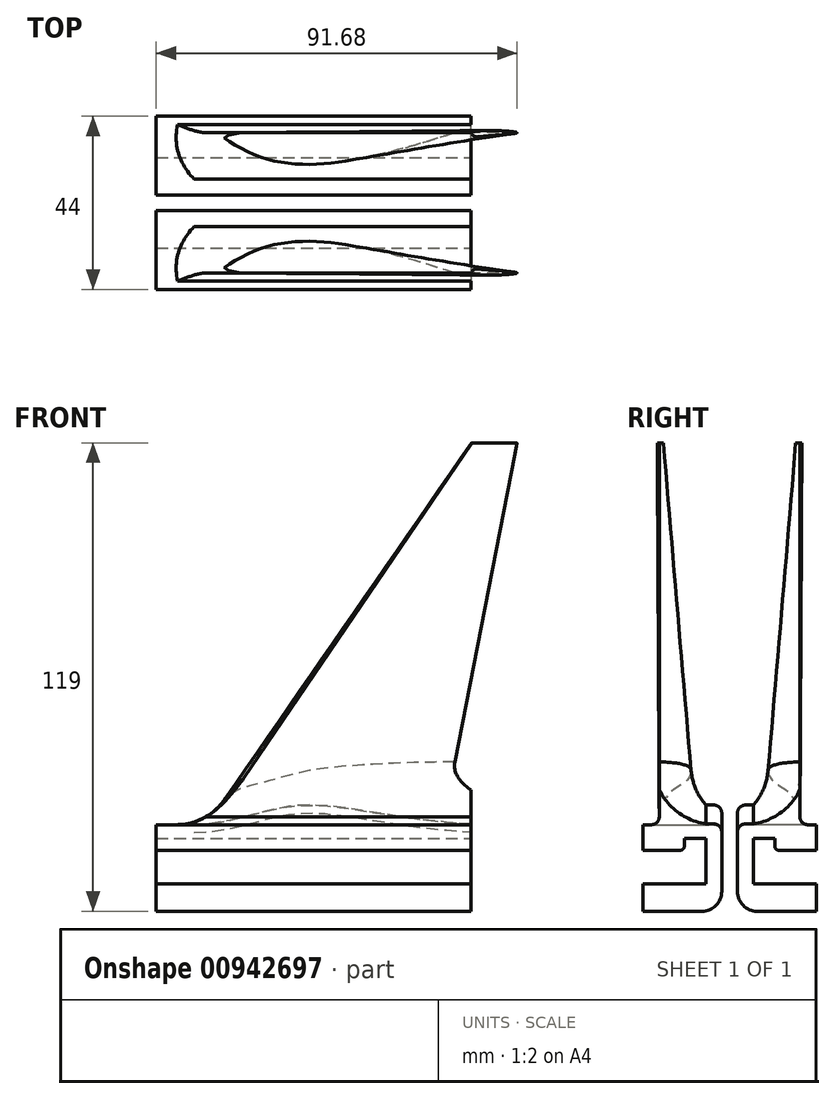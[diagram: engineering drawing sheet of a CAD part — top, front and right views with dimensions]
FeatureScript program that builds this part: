
annotation { "Feature Type Name" : "Feature", "Feature Type Description" : "" }
export const myFeature = defineFeature(function(context is Context, id is Id, definition is map)
    precondition{}
    {
        {
            var Q0;
            Q0=qCreatedBy(makeId("Top.planeOp"),FACE);
            var sketch = newSketch(context, id + "F0", { "sketchPlane" : qUnion([Q0])});
            skLineSegment(sketch, "E0", {"start": v(-25.45, 0) * mm, "end": v(34.55, 0) * mm});
            skFitSpline(sketch, "E1", {"points": [v(-25.45, 0) * mm, v(-20.57, 6.59) * mm, v(0, 8.98) * mm, v(34.55, 0) * mm], "startDerivative": vector(-50.24, 16.53) * mm, "endDerivative": vector(98.45, -32) * mm});
            skSolve(sketch);
        }
        {
            var Q0;
            Q0=qCreatedBy(makeId("Top.planeOp"),FACE);
            cPlane(context, id + "F1", {"entities" : qUnion([Q0]), "cplaneType" : CPlaneType.OFFSET, "offset" : 100 * mm, "width" : 150 * mm, "height" : 150 * mm});
        }
        {
            var Q0;
            Q0=qCreatedBy(id+"F1.planeOp",FACE);
            var sketch = newSketch(context, id + "F2", { "sketchPlane" : qUnion([Q0])});
            skFitSpline(sketch, "E2", {"points": [v(43.22, 0.93) * mm, v(45.42, 0.93) * mm, v(54, 0) * mm, v(42.54, 0) * mm, v(43.22, 0.93) * mm]});
            skLineSegment(sketch, "E3", {"start": v(42.54, 0) * mm, "end": v(54, 0) * mm});
            skSolve(sketch);
        }
        {
            var Q0;
            Q0=qSketchRegion(id+"F2",true);
            var Q1;
            Q1=qSketchRegion(id+"F0",true);
            loft(context, id + "F3", {"sheetProfilesArray" : [{ "sheetProfileEntities" : qUnion([Q0]) }, { "sheetProfileEntities" : qUnion([Q1]) }]});
        }
        {
            var Q0;
            Q0=makeQuery(id+"F0.imprint","IMPRINT",FACE,{"disambiguationData":[TD([[makeQuery(id+"F0.imprint","IMPRINT",EDGE,{"derivedFrom":sQuery(id+"F0.wireOp",EDGE,"E0")}),1.0]])]});
            var sketch = newSketch(context, id + "F4", { "sketchPlane" : qUnion([Q0])});
            skLineSegment(sketch, "E4.bottom", {"start": v(-37.64, -4.14) * mm, "end": v(42.36, -4.14) * mm});
            skLineSegment(sketch, "E4.top", {"start": v(-37.64, 11.86) * mm, "end": v(42.36, 11.86) * mm});
            skLineSegment(sketch, "E4.left", {"start": v(-37.64, -4.14) * mm, "end": v(-37.64, 11.86) * mm});
            skLineSegment(sketch, "E4.right", {"start": v(42.36, -4.14) * mm, "end": v(42.36, 11.86) * mm});
            skLineSegment(sketch, "E5", {"start": v(-37.64, 3.86) * mm, "end": v(42.36, 3.86) * mm, "construction": true});
            skLineSegment(sketch, "E6", {"start": v(2.36, -4.14) * mm, "end": v(2.36, 11.86) * mm, "construction": true});
            skSolve(sketch);
        }
        {
            var Q0;
            Q0=qSketchRegion(id+"F4",true);
            extrude(context, id + "F5", {"entities" : qUnion([Q0]), "operationType" : NewBodyOperationType.ADD, "depth" : 3 * mm, "offsetDistance" : 25 * mm});
        }
        {
            var Q0;
            Q0=makeQuery(id+"F5.boolean.opBoolean","MERGE",FACE,{"derivedFrom":[makeQuery(id+"F3.opLoft","CAP_FACE",FACE,{"disambiguationData":[OSD([makeQuery(id+"F0.imprint","IMPRINT",FACE,{"disambiguationData":[TD([[makeQuery(id+"F0.imprint","IMPRINT",EDGE,{"derivedFrom":sQuery(id+"F0.wireOp",EDGE,"E0")}),1.0]])]})])],"isStart":true}),makeQuery(id+"F5.opExtrude","CAP_FACE",FACE,{"disambiguationData":[OSD([sQuery(id+"F4.wireOp",EDGE,"E4.bottom"),sQuery(id+"F4.wireOp",EDGE,"E4.top"),sQuery(id+"F4.wireOp",EDGE,"E4.left"),sQuery(id+"F4.wireOp",EDGE,"E4.right")])],"isStart":true})]});
            var sketch = newSketch(context, id + "F6", { "sketchPlane" : qUnion([Q0])});
            skLineSegment(sketch, "E7.bottom", {"start": v(-37.64, 4.14) * mm, "end": v(-22.64, 4.14) * mm});
            skLineSegment(sketch, "E7.top", {"start": v(-37.64, 10.14) * mm, "end": v(-22.64, 10.14) * mm});
            skLineSegment(sketch, "E7.left", {"start": v(-37.64, 4.14) * mm, "end": v(-37.64, 10.14) * mm});
            skLineSegment(sketch, "E7.right", {"start": v(-22.64, 4.14) * mm, "end": v(-22.64, 10.14) * mm});
            skLineSegment(sketch, "E8.bottom", {"start": v(-37.64, -11.86) * mm, "end": v(-22.64, -11.86) * mm});
            skLineSegment(sketch, "E8.top", {"start": v(-37.64, -17.86) * mm, "end": v(-22.64, -17.86) * mm});
            skLineSegment(sketch, "E8.left", {"start": v(-37.64, -11.86) * mm, "end": v(-37.64, -17.86) * mm});
            skLineSegment(sketch, "E8.right", {"start": v(-22.64, -11.86) * mm, "end": v(-22.64, -17.86) * mm});
            skLineSegment(sketch, "E9", {"start": v(-22.64, 4.14) * mm, "end": v(-22.64, -11.86) * mm, "construction": true});
            skLineSegment(sketch, "E10.bottom", {"start": v(42.36, 4.14) * mm, "end": v(27.36, 4.14) * mm});
            skLineSegment(sketch, "E10.top", {"start": v(42.36, 10.14) * mm, "end": v(27.36, 10.14) * mm});
            skLineSegment(sketch, "E10.left", {"start": v(42.36, 4.14) * mm, "end": v(42.36, 10.14) * mm});
            skLineSegment(sketch, "E10.right", {"start": v(27.36, 4.14) * mm, "end": v(27.36, 10.14) * mm});
            skLineSegment(sketch, "E11.bottom", {"start": v(42.36, -11.86) * mm, "end": v(27.36, -11.86) * mm});
            skLineSegment(sketch, "E11.top", {"start": v(42.36, -17.86) * mm, "end": v(27.36, -17.86) * mm});
            skLineSegment(sketch, "E11.left", {"start": v(42.36, -11.86) * mm, "end": v(42.36, -17.86) * mm});
            skLineSegment(sketch, "E11.right", {"start": v(27.36, -11.86) * mm, "end": v(27.36, -17.86) * mm});
            skLineSegment(sketch, "E12", {"start": v(-30.14, 10.14) * mm, "end": v(-30.14, -17.86) * mm, "construction": true});
            skLineSegment(sketch, "E13", {"start": v(-37.64, 7.14) * mm, "end": v(27.36, 7.14) * mm, "construction": true});
            skLineSegment(sketch, "E14", {"start": v(-37.64, -14.86) * mm, "end": v(27.36, -14.86) * mm, "construction": true});
            skCircle(sketch, "E15", {"center": v(-30.14, 7.14) * mm, "radius": 2.2 * mm});
            skCircle(sketch, "E16", {"center": v(-30.14, -14.86) * mm, "radius": 2.2 * mm});
            skLineSegment(sketch, "E17", {"start": v(34.86, 10.14) * mm, "end": v(34.86, -17.86) * mm, "construction": true});
            skLineSegment(sketch, "E18", {"start": v(27.36, 7.14) * mm, "end": v(42.36, 7.14) * mm, "construction": true});
            skLineSegment(sketch, "E19", {"start": v(27.36, -14.86) * mm, "end": v(42.36, -14.86) * mm, "construction": true});
            skCircle(sketch, "E20", {"center": v(34.86, 7.14) * mm, "radius": 2.2 * mm});
            skCircle(sketch, "E21", {"center": v(34.86, -14.86) * mm, "radius": 2.2 * mm});
            skSolve(sketch);
        }
        {
            var Q0;
            {var subQ0=sQuery(id+"F2.wireOp",EDGE,"E2");var subQ1=sQuery(id+"F2.wireOp",EDGE,"E3");var subQ2=sQuery(id+"F0.wireOp",EDGE,"E1");var subQ3=sQuery(id+"F0.wireOp",EDGE,"E0");Q0=makeQuery(id+"F5.boolean.opBoolean","INTERSECT",EDGE,{"derivedFrom":[makeQuery(id+"F3.opLoft","SWEPT_FACE",FACE,{"disambiguationData":[OSD([subQ3,subQ2,subQ0,subQ1]),TDD([makeQuery(id+"F0.imprint","INTERSECT",VERTEX,{"disambiguationData":[OD(0.0)],"derivedFrom":[subQ3,subQ2]}),makeQuery(id+"F0.imprint","INTERSECT",VERTEX,{"disambiguationData":[OD(1.0)],"derivedFrom":[subQ3,subQ2]}),makeQuery(id+"F0.imprint","IMPRINT",EDGE,{"derivedFrom":subQ2}),makeQuery(id+"F2.imprint","INTERSECT",VERTEX,{"disambiguationData":[OD(0.0)],"derivedFrom":[subQ0,subQ1]}),makeQuery(id+"F2.imprint","INTERSECT",VERTEX,{"disambiguationData":[OD(1.0)],"derivedFrom":[subQ0,subQ1]}),makeQuery(id+"F2.imprint","IMPRINT",EDGE,{"derivedFrom":subQ0})])]}),makeQuery(id+"F5.opExtrude","CAP_FACE",FACE,{"disambiguationData":[OSD([sQuery(id+"F4.wireOp",EDGE,"E4.bottom"),sQuery(id+"F4.wireOp",EDGE,"E4.top"),sQuery(id+"F4.wireOp",EDGE,"E4.left"),sQuery(id+"F4.wireOp",EDGE,"E4.right")])],"isStart":false})]});}
            fillet(context, id + "F7", {"entities" : qUnion([Q0]), "radius" : 15 * mm, "tangentPropagation" : true, "allowEdgeOverflow" : false});
        }
        {
            var Q0;
            Q0=makeQuery(id+"F5.opExtrude","SWEPT_FACE",FACE,{"disambiguationData":[OSD([sQuery(id+"F4.wireOp",EDGE,"E4.top")])]});
            extrude(context, id + "F8", {"entities" : qUnion([Q0]), "operationType" : NewBodyOperationType.ADD, "depth" : 4 * mm, "offsetDistance" : 25 * mm});
        }
        {
            var Q0;
            Q0=makeQuery(id+"F1JkRQICYIVjqss_1.boolean.opBoolean","MERGE",FACE,{"derivedFrom":[makeQuery(id+"F8.opExtrude","CAP_FACE",FACE,{"disambiguationData":[OSD([sQuery(id+"F4.wireOp",EDGE,"E4.top")])],"isStart":false}),makeQuery(id+"F1JkRQICYIVjqss_1.opExtrude","SWEPT_FACE",FACE,{"disambiguationData":[OSD([sQuery(id+"F0v1QYwDrY6xO1k_1.wireOp",EDGE,"EkqD9QSM-mrW7-2H4G-hvlJ-36K5oW6BhZ5I.bottom")])]})]});
            var sketch = newSketch(context, id + "F9", { "sketchPlane" : qUnion([Q0])});
            skLineSegment(sketch, "E22.bottom", {"start": v(-55.34, 0) * mm, "end": v(44.66, 0) * mm});
            skLineSegment(sketch, "E22.top", {"start": v(-55.34, 3) * mm, "end": v(44.66, 3) * mm});
            skLineSegment(sketch, "E22.left", {"start": v(-55.34, 0) * mm, "end": v(-55.34, 3) * mm});
            skLineSegment(sketch, "E22.right", {"start": v(44.66, 0) * mm, "end": v(44.66, 3) * mm});
            skSolve(sketch);
        }
        {
            var Q0;
            {var subQ3=sQuery(id+"F6.wireOp",EDGE,"E7.bottom");Q0=makeQuery(id+"F6.imprint","IMPRINT",FACE,{"disambiguationData":[TD([[makeQuery(id+"F6.imprint","IMPRINT",EDGE,{"derivedFrom":subQ3}),-1.0]])]});}
            var sketch = newSketch(context, id + "F10", { "sketchPlane" : qUnion([Q0])});
            skLineSegment(sketch, "E23.bottom", {"start": v(42.36, -15.86) * mm, "end": v(-37.64, -15.86) * mm});
            skLineSegment(sketch, "E23.top", {"start": v(42.36, -10.21) * mm, "end": v(-37.64, -10.21) * mm});
            skLineSegment(sketch, "E23.left", {"start": v(42.36, -15.86) * mm, "end": v(42.36, -10.21) * mm});
            skLineSegment(sketch, "E23.right", {"start": v(-37.64, -15.86) * mm, "end": v(-37.64, -10.21) * mm});
            skSolve(sketch);
        }
        {
            var Q0;
            Q0=qSketchRegion(id+"F10",true);
            extrude(context, id + "F11", {"entities" : qUnion([Q0]), "operationType" : NewBodyOperationType.ADD, "depth" : 13 * mm, "offsetDistance" : 25 * mm});
        }
        {
            var Q0;
            Q0=makeQuery(id+"F11.opExtrude","SWEPT_FACE",FACE,{"disambiguationData":[OSD([sQuery(id+"F10.wireOp",EDGE,"E23.top")])]});
            var sketch = newSketch(context, id + "F12", { "sketchPlane" : qUnion([Q0])});
            skLineSegment(sketch, "E24.bottom", {"start": v(-37.64, -13) * mm, "end": v(42.36, -13) * mm});
            skLineSegment(sketch, "E24.top", {"start": v(-37.64, -9.57) * mm, "end": v(42.36, -9.57) * mm});
            skLineSegment(sketch, "E24.left", {"start": v(-37.64, -13) * mm, "end": v(-37.64, -9.57) * mm});
            skLineSegment(sketch, "E24.right", {"start": v(42.36, -13) * mm, "end": v(42.36, -9.57) * mm});
            skSolve(sketch);
        }
        {
            var Q0;
            Q0=qSketchRegion(id+"F12",true);
            extrude(context, id + "F13", {"entities" : qUnion([Q0]), "operationType" : NewBodyOperationType.ADD, "depth" : 4 * mm, "offsetDistance" : 25 * mm});
        }
        {
            var Q0;
            {var subQ0=sQuery(id+"F4.wireOp",EDGE,"E4.right");Q0=makeQuery(id+"F13.boolean.opBoolean","MERGE",FACE,{"derivedFrom":[makeQuery(id+"F11.boolean.opBoolean","MERGE",FACE,{"derivedFrom":[makeQuery(id+"F8.boolean.opBoolean","MERGE",FACE,{"derivedFrom":[makeQuery(id+"F5.opExtrude","SWEPT_FACE",FACE,{"disambiguationData":[OSD([subQ0])]}),makeQuery(id+"F8.opExtrude","SWEPT_FACE",FACE,{"disambiguationData":[OSD([sQuery(id+"F4.wireOp",EDGE,"E4.top"),subQ0])]})]}),makeQuery(id+"F11.opExtrude","SWEPT_FACE",FACE,{"disambiguationData":[OSD([sQuery(id+"F10.wireOp",EDGE,"E23.left")])]})]}),makeQuery(id+"F13.opExtrude","SWEPT_FACE",FACE,{"disambiguationData":[OSD([sQuery(id+"F12.wireOp",EDGE,"E24.right")])]})]});}
            var sketch = newSketch(context, id + "F14", { "sketchPlane" : qUnion([Q0])});
            skLineSegment(sketch, "E25.bottom", {"start": v(15.86, -13) * mm, "end": v(-4.14, -13) * mm});
            skLineSegment(sketch, "E25.top", {"start": v(15.86, 0) * mm, "end": v(-4.14, 0) * mm});
            skLineSegment(sketch, "E25.left", {"start": v(15.86, -13) * mm, "end": v(15.86, 0) * mm});
            skLineSegment(sketch, "E25.right", {"start": v(-4.14, -13) * mm, "end": v(-4.14, 0) * mm});
            skSolve(sketch);
        }
        {
            var Q0;
            Q0 = qSketchRegion(id + "F14", true);
            var Q1;
            {var subQ0=sQuery(id+"F4.wireOp",EDGE,"E4.left");Q1=makeQuery(id+"F13.boolean.opBoolean","MERGE",FACE,{"derivedFrom":[makeQuery(id+"F11.boolean.opBoolean","MERGE",FACE,{"derivedFrom":[makeQuery(id+"F8.boolean.opBoolean","MERGE",FACE,{"derivedFrom":[makeQuery(id+"F5.opExtrude","SWEPT_FACE",FACE,{"disambiguationData":[OSD([subQ0])]}),makeQuery(id+"F8.opExtrude","SWEPT_FACE",FACE,{"disambiguationData":[OSD([sQuery(id+"F4.wireOp",EDGE,"E4.top"),subQ0])]})]}),makeQuery(id+"F11.opExtrude","SWEPT_FACE",FACE,{"disambiguationData":[OSD([sQuery(id+"F10.wireOp",EDGE,"E23.right")])]})]}),makeQuery(id+"F13.opExtrude","SWEPT_FACE",FACE,{"disambiguationData":[OSD([sQuery(id+"F12.wireOp",EDGE,"E24.left")])]})]});}
            extrude(context, id + "F15", {"entities" : qUnion([Q0]), "operationType" : NewBodyOperationType.ADD, "endBound" : BoundingType.UP_TO_SURFACE, "oppositeDirection" : true, "depth" : 25 * mm, "endBoundEntityFace" : qUnion([Q1]), "offsetDistance" : 25 * mm});
        }
        {
            var Q0;
            Q0=makeQuery(id+"F15.boolean.opBoolean","MERGE",FACE,{"derivedFrom":[makeQuery(id+"F5.opExtrude","SWEPT_FACE",FACE,{"disambiguationData":[OSD([sQuery(id+"F4.wireOp",EDGE,"E4.bottom")])]}),makeQuery(id+"F15.opExtrude","SWEPT_FACE",FACE,{"disambiguationData":[OSD([sQuery(id+"F14.wireOp",EDGE,"E25.right")])]})]});
            extrude(context, id + "F16", {"entities" : qUnion([Q0]), "operationType" : NewBodyOperationType.ADD, "surfaceOperationType" : NewSurfaceOperationType.ADD, "depth" : 5 * mm, "offsetDistance" : 25 * mm});
        }
        {
            var Q0;
            {var subQ0=sQuery(id+"F14.wireOp",EDGE,"E25.bottom");Q0=makeQuery(id+"F16.boolean.opBoolean","MERGE",FACE,{"derivedFrom":[makeQuery(id+"F15.boolean.opBoolean","MERGE",FACE,{"derivedFrom":[makeQuery(id+"F13.boolean.opBoolean","MERGE",FACE,{"derivedFrom":[makeQuery(id+"F11.opExtrude","CAP_FACE",FACE,{"disambiguationData":[OSD([sQuery(id+"F10.wireOp",EDGE,"E23.bottom"),sQuery(id+"F10.wireOp",EDGE,"E23.top"),sQuery(id+"F10.wireOp",EDGE,"E23.left"),sQuery(id+"F10.wireOp",EDGE,"E23.right")])],"isStart":false}),makeQuery(id+"F13.opExtrude","SWEPT_FACE",FACE,{"disambiguationData":[OSD([sQuery(id+"F12.wireOp",EDGE,"E24.bottom")])]})]}),makeQuery(id+"F15.opExtrude","SWEPT_FACE",FACE,{"disambiguationData":[OSD([subQ0])]})]}),makeQuery(id+"F16.opExtrude","SWEPT_FACE",FACE,{"disambiguationData":[OSD([subQ0,sQuery(id+"F14.wireOp",EDGE,"E25.right")])]})]});}
            extrude(context, id + "F17", {"entities" : qUnion([Q0]), "operationType" : NewBodyOperationType.ADD, "depth" : 3 * mm, "offsetDistance" : 25 * mm});
        }
        {
            var Q0;
            {var subQ0=sQuery(id+"F14.wireOp",EDGE,"E25.right");var subQ1=sQuery(id+"F14.wireOp",EDGE,"E25.bottom");var subQ2=sQuery(id+"F12.wireOp",EDGE,"E24.right");var subQ3=sQuery(id+"F10.wireOp",EDGE,"E23.left");var subQ4=sQuery(id+"F4.wireOp",EDGE,"E4.right");Q0=makeQuery(id+"F17.boolean.opBoolean","MERGE",FACE,{"derivedFrom":[makeQuery(id+"F16.boolean.opBoolean","MERGE",FACE,{"derivedFrom":[makeQuery(id+"F15.boolean.opBoolean","MERGE",FACE,{"derivedFrom":[makeQuery(id+"F13.boolean.opBoolean","MERGE",FACE,{"derivedFrom":[makeQuery(id+"F11.boolean.opBoolean","MERGE",FACE,{"derivedFrom":[makeQuery(id+"F8.boolean.opBoolean","MERGE",FACE,{"derivedFrom":[makeQuery(id+"F5.opExtrude","SWEPT_FACE",FACE,{"disambiguationData":[OSD([subQ4])]}),makeQuery(id+"F8.opExtrude","SWEPT_FACE",FACE,{"disambiguationData":[OSD([sQuery(id+"F4.wireOp",EDGE,"E4.top"),subQ4])]})]}),makeQuery(id+"F11.opExtrude","SWEPT_FACE",FACE,{"disambiguationData":[OSD([subQ3])]})]}),makeQuery(id+"F13.opExtrude","SWEPT_FACE",FACE,{"disambiguationData":[OSD([subQ2])]})]}),makeQuery(id+"F15.opExtrude","CAP_FACE",FACE,{"disambiguationData":[OSD([subQ1,sQuery(id+"F14.wireOp",EDGE,"E25.top"),sQuery(id+"F14.wireOp",EDGE,"E25.left"),subQ0])],"isStart":true})]}),makeQuery(id+"F16.opExtrude","SWEPT_FACE",FACE,{"disambiguationData":[OSD([sQuery(id+"F4.wireOp",EDGE,"E4.bottom"),subQ4,subQ0])]})]}),makeQuery(id+"F17.opExtrude","SWEPT_FACE",FACE,{"disambiguationData":[OSD([subQ3,sQuery(id+"F12.wireOp",EDGE,"E24.bottom"),subQ2,subQ1,subQ0])]})]});}
            var sketch = newSketch(context, id + "F18", { "sketchPlane" : qUnion([Q0])});
            skLineSegment(sketch, "E26", {"start": v(-9.14, -12) * mm, "end": v(11.86, -12) * mm});
            skLineSegment(sketch, "E27", {"start": v(11.86, -12) * mm, "end": v(11.86, -0.5) * mm});
            skLineSegment(sketch, "E28", {"start": v(11.86, -0.5) * mm, "end": v(6.36, -0.5) * mm});
            skLineSegment(sketch, "E29", {"start": v(6.36, -0.5) * mm, "end": v(6.36, -2.5) * mm});
            skLineSegment(sketch, "E30", {"start": v(5.36, -3.5) * mm, "end": v(-9.14, -3.5) * mm});
            skPoint(sketch, "E31.visualSharp", {"position": v(6.36, -3.5) * mm});
            skArc(sketch, "E31.filletArc", {"start": v(5.36, -3.5) * mm, "mid": v(6.06, -3.2) * mm, "end": v(6.36, -2.5) * mm});
            skLineSegment(sketch, "E32", {"start": v(-9.14, -3.5) * mm, "end": v(-9.14, -12) * mm});
            skSolve(sketch);
        }
        {
            var Q0;
            Q0 = qSketchRegion(id + "F18", true);
            extrude(context, id + "F19", {"entities" : qUnion([Q0]), "operationType" : NewBodyOperationType.REMOVE, "endBound" : BoundingType.THROUGH_ALL, "oppositeDirection" : true, "depth" : 25 * mm, "offsetDistance" : 25 * mm});
        }
        {
            var Q0;
            Q0=makeQuery(id+"F11.opExtrude","CAP_EDGE",EDGE,{"disambiguationData":[OSD([sQuery(id+"F10.wireOp",EDGE,"E23.bottom")])],"isStart":false});
            var Q1;
            Q1=makeQuery(id+"F8.opExtrude","CAP_EDGE",EDGE,{"disambiguationData":[OSD([sQuery(id+"F0.wireOp",EDGE,"E0"),sQuery(id+"F0.wireOp",EDGE,"E1"),sQuery(id+"F2.wireOp",EDGE,"E2"),sQuery(id+"F2.wireOp",EDGE,"E3"),sQuery(id+"F4.wireOp",EDGE,"E4.bottom"),sQuery(id+"F4.wireOp",EDGE,"E4.top"),sQuery(id+"F4.wireOp",EDGE,"E4.left"),sQuery(id+"F4.wireOp",EDGE,"E4.right")])],"isStart":false});
            var Q2;
            Q2=makeQuery(id+"F5.opExtrude","CAP_EDGE",EDGE,{"disambiguationData":[OSD([sQuery(id+"F4.wireOp",EDGE,"E4.bottom")])],"isStart":false});
            fillet(context, id + "F20", {"entities" : qUnion([Q0, Q1, Q2]), "radius" : 2 * mm, "tangentPropagation" : true, "allowEdgeOverflow" : false});
        }
        {
            var Q0;
            {var subQ0=sQuery(id+"F2.wireOp",EDGE,"E3");var subQ1=sQuery(id+"F2.wireOp",EDGE,"E2");var subQ2=sQuery(id+"F0.wireOp",EDGE,"E0");var subQ3=sQuery(id+"F0.wireOp",EDGE,"E1");Q0=makeQuery(id+"F5.boolean.opBoolean","INTERSECT",EDGE,{"derivedFrom":[makeQuery(id+"F3.opLoft","SWEPT_FACE",FACE,{"disambiguationData":[OSD([subQ2,subQ3,subQ1,subQ0]),TDD([makeQuery(id+"F0.imprint","INTERSECT",VERTEX,{"disambiguationData":[OD(0.0)],"derivedFrom":[subQ2,subQ3]}),makeQuery(id+"F0.imprint","INTERSECT",VERTEX,{"disambiguationData":[OD(1.0)],"derivedFrom":[subQ2,subQ3]}),makeQuery(id+"F0.imprint","IMPRINT",EDGE,{"derivedFrom":subQ2}),makeQuery(id+"F2.imprint","INTERSECT",VERTEX,{"disambiguationData":[OD(0.0)],"derivedFrom":[subQ1,subQ0]}),makeQuery(id+"F2.imprint","INTERSECT",VERTEX,{"disambiguationData":[OD(1.0)],"derivedFrom":[subQ1,subQ0]}),makeQuery(id+"F2.imprint","IMPRINT",EDGE,{"derivedFrom":subQ0})])]}),makeQuery(id+"F5.opExtrude","CAP_FACE",FACE,{"disambiguationData":[OSD([sQuery(id+"F4.wireOp",EDGE,"E4.bottom"),sQuery(id+"F4.wireOp",EDGE,"E4.top"),sQuery(id+"F4.wireOp",EDGE,"E4.left"),sQuery(id+"F4.wireOp",EDGE,"E4.right")])],"isStart":false})]});}
            fillet(context, id + "F21", {"entities" : qUnion([Q0]), "radius" : 2 * mm, "tangentPropagation" : true, "allowEdgeOverflow" : false});
        }
        {
            var Q0;
            {var subQ4=sQuery(id+"F4.wireOp",EDGE,"E4.bottom");var subQ5=sQuery(id+"F14.wireOp",EDGE,"E25.right");var subQ6=sQuery(id+"F14.wireOp",EDGE,"E25.bottom");Q0=makeQuery(id+"F19.boolean.opBoolean","SPLIT",FACE,{"disambiguationData":[TD([makeQuery(id+"F16.opExtrude","SWEPT_FACE",FACE,{"disambiguationData":[OSD([subQ4])]})])],"derivedFrom":makeQuery(id+"F17.boolean.opBoolean","MERGE",FACE,{"derivedFrom":[makeQuery(id+"F16.opExtrude","CAP_FACE",FACE,{"disambiguationData":[OSD([subQ4,subQ5])],"isStart":false}),makeQuery(id+"F17.opExtrude","SWEPT_FACE",FACE,{"disambiguationData":[OSD([subQ6,subQ5])]})]})});}
            var Q1;
            {var subQ0=sQuery(id+"F14.wireOp",EDGE,"E25.right");var subQ3=sQuery(id+"F14.wireOp",EDGE,"E25.bottom");var subQ12=sQuery(id+"F4.wireOp",EDGE,"E4.bottom");Q1=makeQuery(id+"F19.boolean.opBoolean","SPLIT",FACE,{"disambiguationData":[TD([makeQuery(id+"F19.opExtrude","SWEPT_FACE",FACE,{"disambiguationData":[OSD([sQuery(id+"F18.wireOp",EDGE,"E26")])]})])],"derivedFrom":makeQuery(id+"F17.boolean.opBoolean","MERGE",FACE,{"derivedFrom":[makeQuery(id+"F16.opExtrude","CAP_FACE",FACE,{"disambiguationData":[OSD([subQ12,subQ0])],"isStart":false}),makeQuery(id+"F17.opExtrude","SWEPT_FACE",FACE,{"disambiguationData":[OSD([subQ3,subQ0])]})]})});}
            extrude(context, id + "F22", {"entities" : qUnion([Q0, Q1]), "operationType" : NewBodyOperationType.REMOVE, "oppositeDirection" : true, "depth" : 5 * mm, "offsetDistance" : 25 * mm});
        }
        {
            var Q0;
            Q0=makeQuery(id+"F17.opExtrude","CAP_FACE",FACE,{"disambiguationData":[OSD([sQuery(id+"F10.wireOp",EDGE,"E23.bottom"),sQuery(id+"F10.wireOp",EDGE,"E23.top"),sQuery(id+"F10.wireOp",EDGE,"E23.left"),sQuery(id+"F10.wireOp",EDGE,"E23.right"),sQuery(id+"F12.wireOp",EDGE,"E24.bottom"),sQuery(id+"F14.wireOp",EDGE,"E25.bottom"),sQuery(id+"F14.wireOp",EDGE,"E25.right")])],"isStart":false});
            extrude(context, id + "F23", {"entities" : qUnion([Q0]), "operationType" : NewBodyOperationType.ADD, "depth" : 3 * mm, "offsetDistance" : 25 * mm});
        }
        {
            var Q0;
            Q0=makeQuery(id+"F23.opExtrude","CAP_EDGE",EDGE,{"disambiguationData":[OSD([sQuery(id+"F10.wireOp",EDGE,"E23.bottom")])],"isStart":false});
            fillet(context, id + "F24", {"entities" : qUnion([Q0]), "radius" : 5 * mm, "tangentPropagation" : true, "allowEdgeOverflow" : false});
        }
        {
            var Q0;
            Q0=makeQuery(id+"F11.boolean.opBoolean","MERGE",FACE,{"derivedFrom":[makeQuery(id+"F8.opExtrude","CAP_FACE",FACE,{"disambiguationData":[OSD([sQuery(id+"F4.wireOp",EDGE,"E4.top")])],"isStart":false}),makeQuery(id+"F11.opExtrude","SWEPT_FACE",FACE,{"disambiguationData":[OSD([sQuery(id+"F10.wireOp",EDGE,"E23.bottom")])]})]});
            cPlane(context, id + "F25", {"entities" : qUnion([Q0]), "cplaneType" : CPlaneType.OFFSET, "offset" : 2 * mm, "width" : 150 * mm, "height" : 150 * mm});
        }
        {
            var Q0;
            Q0=makeQuery(id+"F3.opLoft","SWEPT_BODY",BODY,{"disambiguationData":[OSD([makeQuery(id+"F0.imprint","IMPRINT",FACE,{"disambiguationData":[TD([[makeQuery(id+"F0.imprint","IMPRINT",EDGE,{"derivedFrom":sQuery(id+"F0.wireOp",EDGE,"E0")}),1.0]])]}),makeQuery(id+"F2.imprint","IMPRINT",FACE,{"disambiguationData":[TD([[makeQuery(id+"F2.imprint","IMPRINT",EDGE,{"derivedFrom":sQuery(id+"F2.wireOp",EDGE,"E2")}),-1.0]])]})])]});
            var Q1;
            Q1=qCreatedBy(id+"F25.planeOp",FACE);
            mirror(context, id + "F26", {"entities" : qUnion([Q0]), "mirrorPlane" : qUnion([Q1])});
        }
    });
